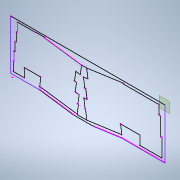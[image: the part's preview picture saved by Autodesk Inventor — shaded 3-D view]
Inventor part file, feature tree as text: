
AUTODESK INVENTOR PART (.ipt)
format: ipt  version: 2022 (Build 260153000, 153)  size: 138,752 bytes
history: native  units: in
note: dims shown in document units (in); Inventor stores cm internally (conversion verified against a paired STEP export)
features: plane x1, sketch x1
ambient origin geometry x8: Origin, YZ Plane, XZ Plane, XY Plane, X Axis, Y Axis, Z Axis, Center Point
feature tree (2):
  plane  "Work Plane1"
  sketch  "Sketch1"
